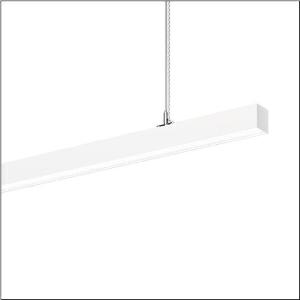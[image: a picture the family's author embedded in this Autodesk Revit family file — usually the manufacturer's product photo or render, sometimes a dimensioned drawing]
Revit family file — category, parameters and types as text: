
# Revit family: silica_r__21_51mx33da37wb_a2a9
name_source: partatom
category: Lighting Fixtures
units: mm (PartAtom-declared; Revit-internal decimal feet)

## family parameters
Cut with Voids When Loaded = No
Host = Face
Light Source = No
Part Type = Normal
Room Calculation Point = No
Round Connector Dimension = Use Diameter
Shared = No

## types (1)
- --- (1 x LED, 5910 lm, 41.3 W, 3000K)
    Apparent Load = 41 VA
    CIE Flux Codes = 78 96 99 55 100
    Color Rendering = 80
    Color Temperature = 3000K
    Default Elevation = 1800 mm
    Description = Silica® 21, office luminaire, primary optical cover: prismatic diffuser, of PMMA, CAT 2 (L<= 3000cd/m²), light emission: direct/indirect distribution, primary light characteristic: symmetric, installation type: suspended mounting, LED, rated luminous flux: 5.910lm, luminous efficacy: 143lm/W, light colour: 830, colour temperature: 3000K, with terminal, 3+2-pole, max. 2.5mm², mains connection: 220..240V, AC, 50/60Hz, rated input power: 41.3W, luminaire housing, of aluminium, traffic white (RAL 9016), length: 1.204mm, width: 53mm, height: 53mm, protection rating (complete): IP20, insulation class (complete): insulation class I (protective earthing), certification: CE, permissible operating ambient temperature: 0..+35°C, standard: EN 50419, packaging unit: 1 piece
    Height = 53 mm
    Lamp = 1 x LED
    Lamp Light Flux = 5910 lm
    Lamp Power = 41.3 W
    Lamp count = 1
    Length = 1204 mm
    Luminous efficacy = 143 lm/W
    Manufacturer = Siteco
    ModVariant = No
    Model = 51MX33DA37WB
    Mounting Place = Ceiling
    Mounting Type = Pendant
    Number of Poles = 1
    OnlyDefault = Yes
    Power Factor = 1
    Product Name = Silica® 21
    Product group = office luminaire | ceiling pendant
    ProductGroupID = 902
    Protection Class = Protection class I
    Protection Degree = IP 20
    RLX_Detail_Level = 1
    RLX_Emergency_Light_Flux = 0 lm
    RLX_Emergency_Type = 0
    RLX_Emergency_Type_DB = No
    RlxData = <blob elided: 21393 chars, md5=55bfae44>
    Socket = socket
    Standby Power = 0 W
    System Light Flux = 5910 lm
    System Power = 41 W
    Type Comments = factory setting: luminous flux: 100 % | dim-lin: 254 | 345 mA
    Type Image = l_1313629.jpg
    URL = http://relux.com
    VarID = @adj_067395
    Voltage = 0 V
    Weight = 0.00 kg
    Width = 53 mm

## geometry (parser evidence)
native form markers: Blend x4, Sweep x13
no freeform markers — native parametric forms only
